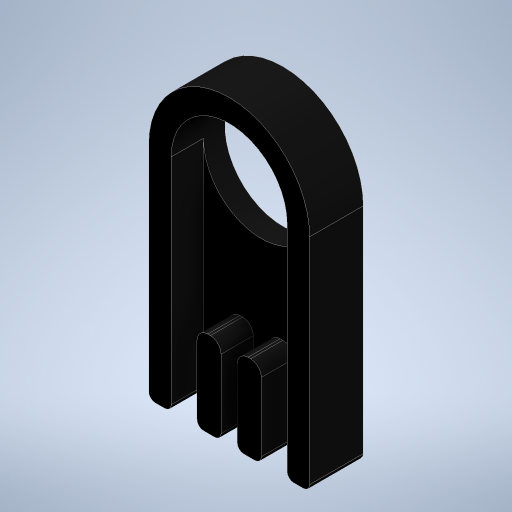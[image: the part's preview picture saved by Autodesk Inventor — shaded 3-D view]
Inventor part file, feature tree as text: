
AUTODESK INVENTOR PART (.ipt)
format: ipt  version: 2024.2 (Build 282272000, 272)  size: 309,760 bytes
history: native  units: mm
features: extrude x2, other x1, sketch x1, fillet x1
ambient origin geometry x8: Origin, YZ Plane, XZ Plane, XY Plane, X Axis, Y Axis, Z Axis, Center Point
bodies: Body1 (feature_tree)
feature tree (5):
  other  "Bryła1"
  sketch  "Szkic1"
  extrude  "Wyciągnięcie proste1"  Depth=10.8mm
  extrude  "Wyciągnięcie proste2"  Depth=12.6mm
  fillet  "Zaokrąglenie1"  Radius=4.0mm
